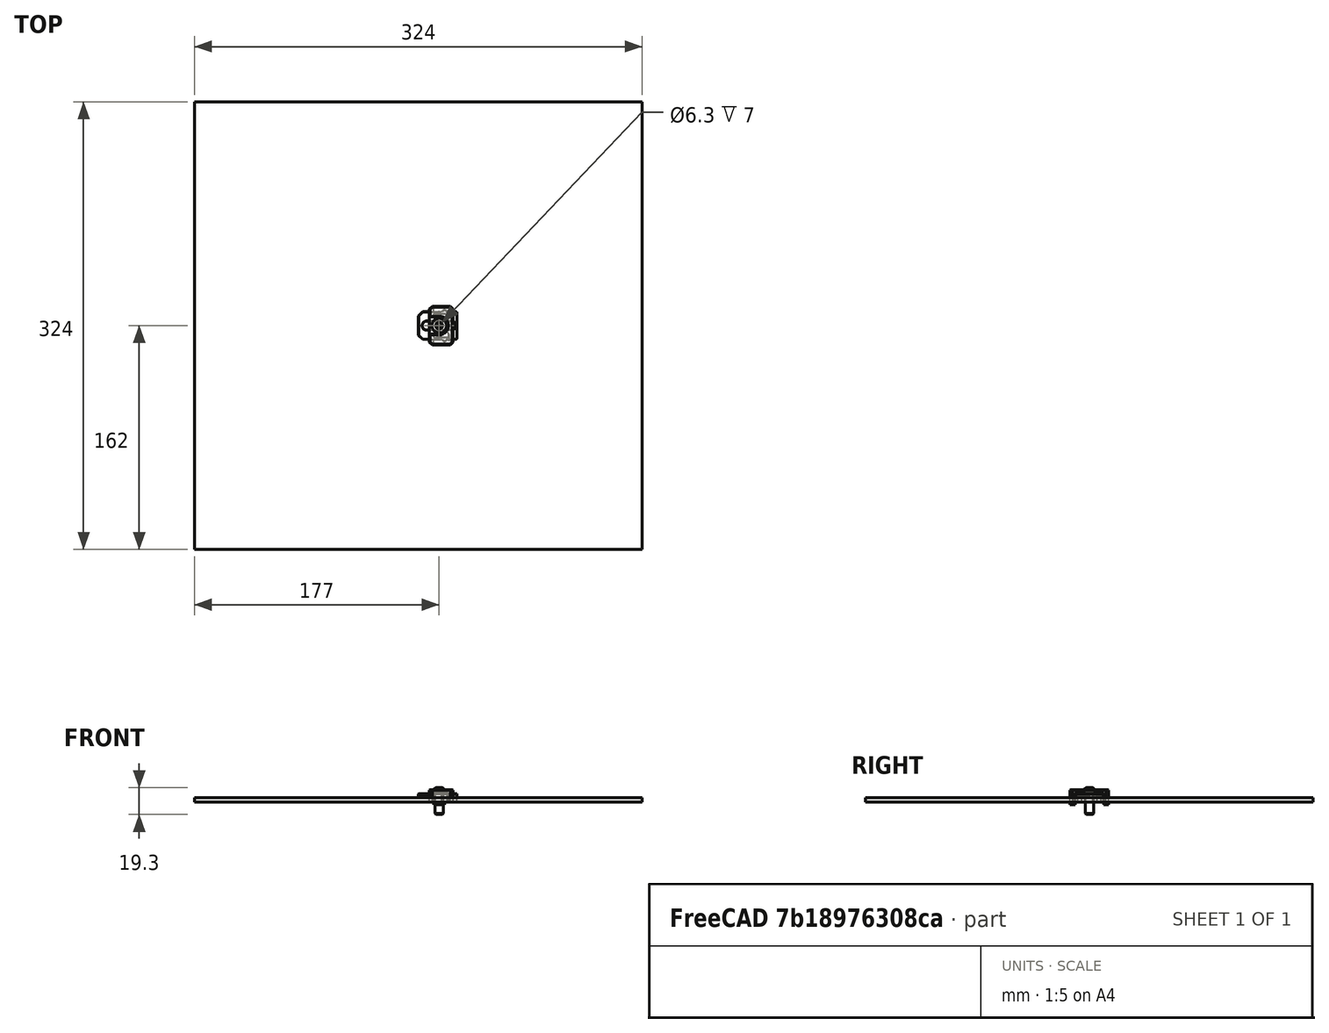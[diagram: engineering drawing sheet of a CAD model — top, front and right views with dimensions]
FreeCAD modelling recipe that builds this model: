
FCSTD DOCUMENT  (FreeCAD 0.19R24291 (Git))
Label: top-panel-assembly
License: Other
LicenseURL: GPL3
objects: Part::Feature×16, App::Part×9, Part::FeaturePython×8, Part::Box×1
note: 25 computed .brp shape members not serialized (recipe doc carries the construction recipe); baked Part::Feature solids carry a one-line shape summary decoded from their .brp

FEATURE [Part::Box] Box  label="panel-324x234x3mm"
  AttacherType = Attacher::AttachEngine3D
  Height = 3
  Length = 324
  Placement = pos=(-162,-162,0) rot=(0,0,1;0rad)
  Width = 324
FEATURE [Part::Feature] Chamfer008002001002
  shape: bbox 28 x 22 x 6 mm, 82 faces (baked)
FEATURE [Part::Feature] Chamfer008002001003
  shape: bbox 17 x 28 x 11 mm, 53 faces (baked)
FEATURE [Part::FeaturePython] Screw026  label="M6x16-Screw001"  # Fasteners workbench fastener (typed FeaturePython)
  Placement = pos=(15,0,7) rot=(0,0,1;0rad)
  baseObject = -> Chamfer008002001003 [Edge135]
  diameter = 4
  invert = false
  length = 3
  lengthCustom = 16
  matchOuter = false
  offset = 0
  thread = false
  type = 40
FEATURE [App::Part] Part014  label="Panel-mounterr2-001"
  Group = -> [Chamfer008002001002,Chamfer008002001003,Screw026]
  Origin = -> Origin014
  Placement = pos=(155,-121,0) rot=(0,0,1;0rad)
FEATURE [Part::Feature] Chamfer008002001004
  shape: bbox 28 x 22 x 6 mm, 82 faces (baked)
FEATURE [Part::Feature] Chamfer008002001005
  shape: bbox 17 x 28 x 11 mm, 53 faces (baked)
FEATURE [Part::FeaturePython] Screw027  label="M6x16-Screw002"  # Fasteners workbench fastener (typed FeaturePython)
  Placement = pos=(15,0,7) rot=(0,0,1;0rad)
  baseObject = -> Chamfer008002001005 [Edge135]
  diameter = 4
  invert = false
  length = 3
  lengthCustom = 16
  matchOuter = false
  offset = 0
  thread = false
  type = 40
FEATURE [App::Part] Part015  label="Panel-mounterr2-002"
  Group = -> [Chamfer008002001004,Chamfer008002001005,Screw027]
  Origin = -> Origin015
  Placement = pos=(155,121,0) rot=(0,0,1;0rad)
FEATURE [Part::Feature] Chamfer008002001006
  shape: bbox 28 x 22 x 6 mm, 82 faces (baked)
FEATURE [Part::Feature] Chamfer008002001007
  shape: bbox 17 x 28 x 11 mm, 53 faces (baked)
FEATURE [Part::FeaturePython] Screw028  label="M6x16-Screw003"  # Fasteners workbench fastener (typed FeaturePython)
  Placement = pos=(15,0,7) rot=(0,0,1;0rad)
  baseObject = -> Chamfer008002001007 [Edge135]
  diameter = 4
  invert = false
  length = 3
  lengthCustom = 16
  matchOuter = false
  offset = 0
  thread = false
  type = 40
FEATURE [App::Part] Part016  label="Panel-mounterr2-003"
  Group = -> [Chamfer008002001006,Chamfer008002001007,Screw028]
  Origin = -> Origin016
  Placement = pos=(121,155,0) rot=(0,0,1;1.5708rad)
FEATURE [Part::Feature] Chamfer008002001010
  shape: bbox 17 x 28 x 11 mm, 53 faces (baked)
FEATURE [Part::FeaturePython] Screw030  label="M6x16-Screw005"  # Fasteners workbench fastener (typed FeaturePython)
  Placement = pos=(15,0,7) rot=(0,0,1;0rad)
  baseObject = -> Chamfer008002001010 [Edge135]
  diameter = 4
  invert = false
  length = 3
  lengthCustom = 16
  matchOuter = false
  offset = 0
  thread = false
  type = 40
FEATURE [Part::Feature] Chamfer008002001011
  shape: bbox 28 x 22 x 6 mm, 82 faces (baked)
FEATURE [App::Part] Part018  label="Panel-mounterr2-005"
  Group = -> [Chamfer008002001011,Chamfer008002001010,Screw030]
  Origin = -> Origin018
  Placement = pos=(-121,155,0) rot=(0,0,1;1.5708rad)
FEATURE [Part::Feature] Chamfer008002001012
  shape: bbox 17 x 28 x 11 mm, 53 faces (baked)
FEATURE [Part::Feature] Chamfer008002001013
  shape: bbox 28 x 22 x 6 mm, 82 faces (baked)
FEATURE [Part::FeaturePython] Screw031  label="M6x16-Screw006"  # Fasteners workbench fastener (typed FeaturePython)
  Placement = pos=(15,0,7) rot=(0,0,1;0rad)
  baseObject = -> Chamfer008002001012 [Edge135]
  diameter = 4
  invert = false
  length = 3
  lengthCustom = 16
  matchOuter = false
  offset = 0
  thread = false
  type = 40
FEATURE [App::Part] Part019  label="Panel-mounterr2-006"
  Group = -> [Chamfer008002001013,Chamfer008002001012,Screw031]
  Origin = -> Origin019
  Placement = pos=(-155,121,0) rot=(0,0,-1;3.14159rad)
FEATURE [Part::FeaturePython] Screw032  label="M6x16-Screw007"  # Fasteners workbench fastener (typed FeaturePython)
  Placement = pos=(15,0,7) rot=(0,0,1;0rad)
  baseObject = -> Chamfer008002001015 [Edge135]
  diameter = 4
  invert = false
  length = 3
  lengthCustom = 16
  matchOuter = false
  offset = 0
  thread = false
  type = 40
FEATURE [Part::Feature] Chamfer008002001014
  shape: bbox 28 x 22 x 6 mm, 82 faces (baked)
FEATURE [Part::Feature] Chamfer008002001015
  shape: bbox 17 x 28 x 11 mm, 53 faces (baked)
FEATURE [App::Part] Part020  label="Panel-mounterr2-007"
  Group = -> [Chamfer008002001014,Chamfer008002001015,Screw032]
  Origin = -> Origin020
  Placement = pos=(-155,-121,0) rot=(0,0,-1;3.14159rad)
FEATURE [Part::FeaturePython] Screw033  label="M6x16-Screw008"  # Fasteners workbench fastener (typed FeaturePython)
  Placement = pos=(15,0,7) rot=(0,0,1;0rad)
  baseObject = -> Chamfer008002001017 [Edge135]
  diameter = 4
  invert = false
  length = 3
  lengthCustom = 16
  matchOuter = false
  offset = 0
  thread = false
  type = 40
FEATURE [Part::Feature] Chamfer008002001016
  shape: bbox 28 x 22 x 6 mm, 82 faces (baked)
FEATURE [Part::Feature] Chamfer008002001017
  shape: bbox 17 x 28 x 11 mm, 53 faces (baked)
FEATURE [App::Part] Part021  label="Panel-mounterr2-008"
  Group = -> [Chamfer008002001016,Chamfer008002001017,Screw033]
  Origin = -> Origin021
  Placement = pos=(-121,-155,0) rot=(0,0,-1;1.5708rad)
FEATURE [Part::Feature] Chamfer008002001018
  shape: bbox 28 x 22 x 6 mm, 82 faces (baked)
FEATURE [Part::Feature] Chamfer008002001019
  shape: bbox 17 x 28 x 11 mm, 53 faces (baked)
FEATURE [Part::FeaturePython] Screw034  label="M6x16-Screw009"  # Fasteners workbench fastener (typed FeaturePython)
  Placement = pos=(15,0,7) rot=(0,0,1;0rad)
  baseObject = -> Chamfer008002001019 [Edge135]
  diameter = 4
  invert = false
  length = 3
  lengthCustom = 16
  matchOuter = false
  offset = 0
  thread = false
  type = 40
FEATURE [App::Part] Part022  label="Panel-mounterr2-009"
  Group = -> [Chamfer008002001018,Chamfer008002001019,Screw034]
  Origin = -> Origin022
  Placement = pos=(121,-155,0) rot=(0,0,-1;1.5708rad)
FEATURE [App::Part] Part  label="top-panel"
  Group = -> [Box,Part014,Part015,Part016,Part018,Part019,Part020,Part021,Part022]
  Origin = -> Origin
